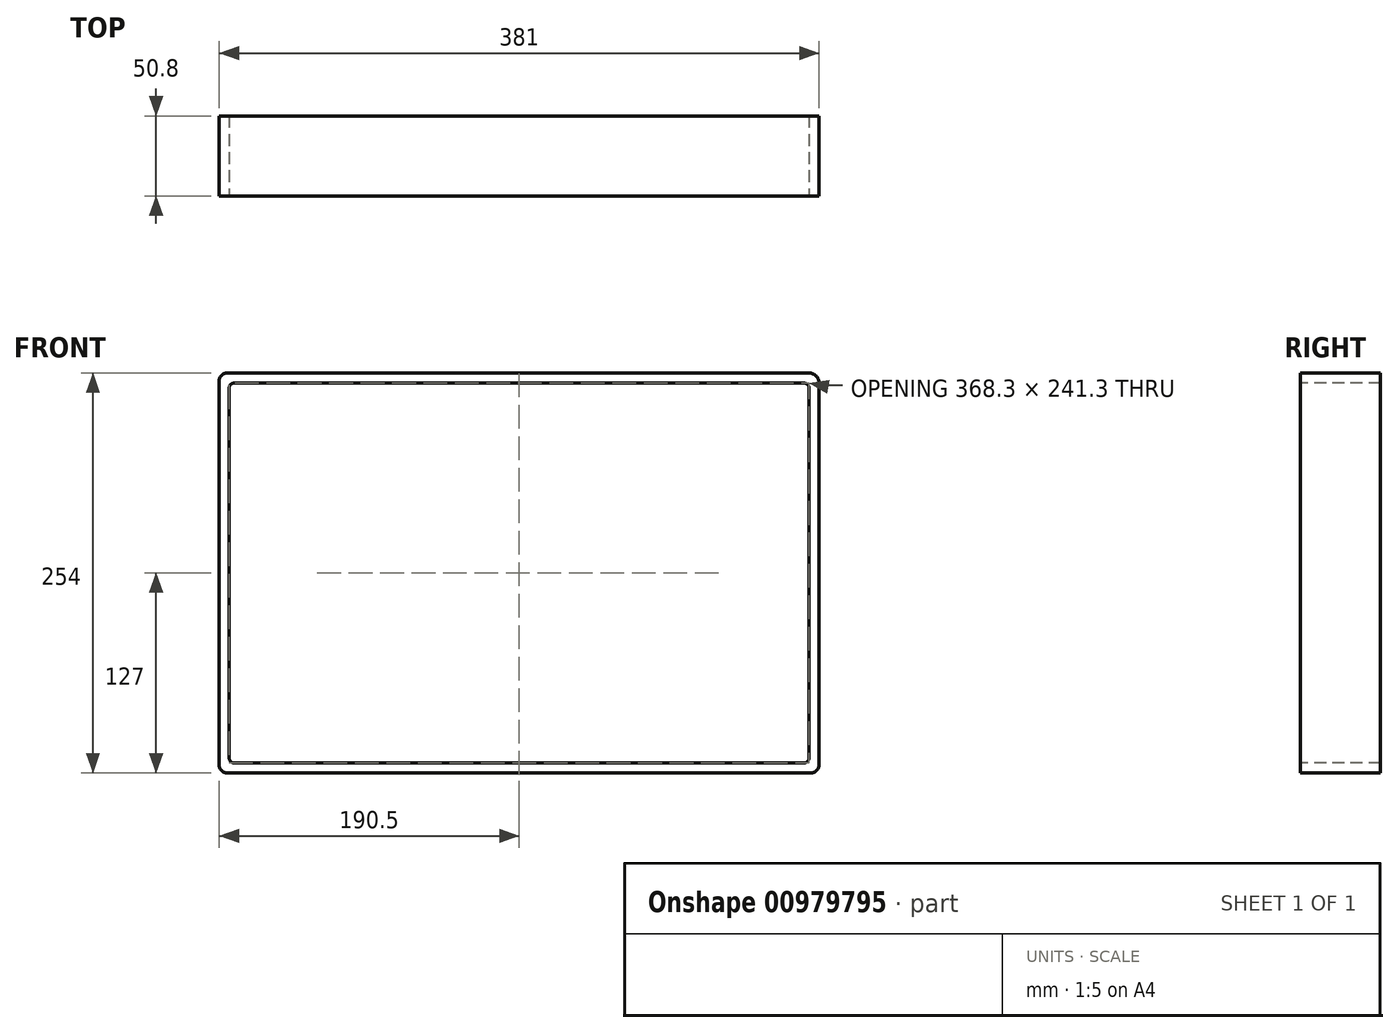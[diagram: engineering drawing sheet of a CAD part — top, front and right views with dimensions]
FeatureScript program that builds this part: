
annotation { "Feature Type Name" : "Feature", "Feature Type Description" : "" }
export const myFeature = defineFeature(function(context is Context, id is Id, definition is map)
    precondition{}
    {
        {
            var Q0;
            Q0=qCreatedBy(makeId("Front.planeOp"),FACE);
            var sketch = newSketch(context, id + "F0", { "sketchPlane" : qUnion([Q0])});
            skLineSegment(sketch, "E0.bottom", {"start": v(190.5, -127) * mm, "end": v(-190.5, -127) * mm});
            skLineSegment(sketch, "E0.top", {"start": v(190.5, 127) * mm, "end": v(-190.5, 127) * mm});
            skLineSegment(sketch, "E0.left", {"start": v(190.5, -127) * mm, "end": v(190.5, 127) * mm});
            skLineSegment(sketch, "E0.right", {"start": v(-190.5, -127) * mm, "end": v(-190.5, 127) * mm});
            skPoint(sketch, "E0.middle", {"position": v(0, 0) * mm});
            skSolve(sketch);
        }
        {
            var Q0;
            Q0=makeQuery(id+"F0.imprint","IMPRINT",FACE,{"disambiguationData":[TD([[makeQuery(id+"F0.imprint","IMPRINT",EDGE,{"derivedFrom":sQuery(id+"F0.wireOp",EDGE,"E0.bottom")}),-1.0]])]});
            extrude(context, id + "F1", {"entities" : qUnion([Q0]), "depth" : 50.8 * mm, "offsetDistance" : 25.4 * mm});
        }
        {
            var Q0;
            Q0=makeQuery(id+"F1.opExtrude","SWEPT_EDGE",EDGE,{"disambiguationData":[OSD([sQuery(id+"F0.wireOp",EDGE,"E0.top"),sQuery(id+"F0.wireOp",EDGE,"E0.left")])]});
            fillet(context, id + "F2", {"entities" : qUnion([Q0]), "radius" : 6.35 * mm, "tangentPropagation" : true, "allowEdgeOverflow" : false});
        }
        {
            var Q0;
            Q0=makeQuery(id+"F1.opExtrude","SWEPT_EDGE",EDGE,{"disambiguationData":[OSD([sQuery(id+"F0.wireOp",EDGE,"E0.bottom"),sQuery(id+"F0.wireOp",EDGE,"E0.left")])]});
            var Q1;
            Q1=makeQuery(id+"F1.opExtrude","SWEPT_EDGE",EDGE,{"disambiguationData":[OSD([sQuery(id+"F0.wireOp",EDGE,"E0.top"),sQuery(id+"F0.wireOp",EDGE,"E0.right")])]});
            var Q2;
            Q2=makeQuery(id+"F1.opExtrude","SWEPT_EDGE",EDGE,{"disambiguationData":[OSD([sQuery(id+"F0.wireOp",EDGE,"E0.bottom"),sQuery(id+"F0.wireOp",EDGE,"E0.right")])]});
            fillet(context, id + "F3", {"entities" : qUnion([Q0, Q1, Q2]), "radius" : 5.08 * mm, "tangentPropagation" : true, "allowEdgeOverflow" : false});
        }
        {
            var Q0;
            Q0=makeQuery(id+"F1.opExtrude","SWEPT_BODY",BODY,{"disambiguationData":[OSD([sQuery(id+"F0.wireOp",EDGE,"E0.bottom"),sQuery(id+"F0.wireOp",EDGE,"E0.top"),sQuery(id+"F0.wireOp",EDGE,"E0.left"),sQuery(id+"F0.wireOp",EDGE,"E0.right")])]});
            transform(context, id + "F4", {"entities" : qUnion([Q0]), "transformType" : TransformType.TRANSLATION_3D, "dx" : 0 * mm, "dy" : 50.8 * mm, "dz" : 0 * mm, "makeCopy" : false});
        }
        {
            var Q0;
            Q0=qCreatedBy(makeId("Front.planeOp"),FACE);
            var sketch = newSketch(context, id + "F5", { "sketchPlane" : qUnion([Q0])});
            skLineSegment(sketch, "E1.bottom", {"start": v(184.15, -120.65) * mm, "end": v(-184.15, -120.65) * mm});
            skLineSegment(sketch, "E1.top", {"start": v(184.15, 120.65) * mm, "end": v(-184.15, 120.65) * mm});
            skLineSegment(sketch, "E1.left", {"start": v(184.15, -120.65) * mm, "end": v(184.15, 120.65) * mm});
            skLineSegment(sketch, "E1.right", {"start": v(-184.15, -120.65) * mm, "end": v(-184.15, 120.65) * mm});
            skPoint(sketch, "E1.middle", {"position": v(0, 0) * mm});
            skSolve(sketch);
        }
        {
            var Q0;
            Q0=makeQuery(id+"F5.imprint","IMPRINT",FACE,{"disambiguationData":[TD([[makeQuery(id+"F5.imprint","IMPRINT",EDGE,{"derivedFrom":sQuery(id+"F5.wireOp",EDGE,"E1.bottom")}),-1.0]])]});
            extrude(context, id + "F6", {"entities" : qUnion([Q0]), "operationType" : NewBodyOperationType.REMOVE, "oppositeDirection" : true, "depth" : 50.8 * mm, "offsetDistance" : 25.4 * mm});
        }
        {
            var Q0;
            Q0=makeQuery(id+"F6.boolean.opBoolean","COPY",EDGE,{"derivedFrom":makeQuery(id+"F6.opExtrude","SWEPT_EDGE",EDGE,{"disambiguationData":[OSD([sQuery(id+"F5.wireOp",EDGE,"E1.bottom"),sQuery(id+"F5.wireOp",EDGE,"E1.right")])]})});
            var Q1;
            Q1=makeQuery(id+"F6.boolean.opBoolean","COPY",EDGE,{"derivedFrom":makeQuery(id+"F6.opExtrude","SWEPT_EDGE",EDGE,{"disambiguationData":[OSD([sQuery(id+"F5.wireOp",EDGE,"E1.top"),sQuery(id+"F5.wireOp",EDGE,"E1.right")])]})});
            var Q2;
            Q2=makeQuery(id+"F6.boolean.opBoolean","COPY",EDGE,{"derivedFrom":makeQuery(id+"F6.opExtrude","SWEPT_EDGE",EDGE,{"disambiguationData":[OSD([sQuery(id+"F5.wireOp",EDGE,"E1.bottom"),sQuery(id+"F5.wireOp",EDGE,"E1.left")])]})});
            var Q3;
            Q3=makeQuery(id+"F6.boolean.opBoolean","COPY",EDGE,{"derivedFrom":makeQuery(id+"F6.opExtrude","SWEPT_EDGE",EDGE,{"disambiguationData":[OSD([sQuery(id+"F5.wireOp",EDGE,"E1.top"),sQuery(id+"F5.wireOp",EDGE,"E1.left")])]})});
            fillet(context, id + "F7", {"entities" : qUnion([Q0, Q1, Q2, Q3]), "radius" : 3.17 * mm, "tangentPropagation" : true, "allowEdgeOverflow" : false});
        }
        {
            var Q0;
            Q0=makeQuery(id+"F1.opExtrude","SWEPT_BODY",BODY,{"disambiguationData":[OSD([sQuery(id+"F0.wireOp",EDGE,"E0.bottom"),sQuery(id+"F0.wireOp",EDGE,"E0.top"),sQuery(id+"F0.wireOp",EDGE,"E0.left"),sQuery(id+"F0.wireOp",EDGE,"E0.right")])]});
            transform(context, id + "F8", {"entities" : qUnion([Q0]), "transformType" : TransformType.TRANSLATION_3D, "dx" : 0 * mm, "dy" : 50.8 * mm, "dz" : 0 * mm, "makeCopy" : false});
        }
        {
            var Q0;
            Q0=makeQuery(id+"F1.opExtrude","SWEPT_BODY",BODY,{"disambiguationData":[OSD([sQuery(id+"F0.wireOp",EDGE,"E0.bottom"),sQuery(id+"F0.wireOp",EDGE,"E0.top"),sQuery(id+"F0.wireOp",EDGE,"E0.left"),sQuery(id+"F0.wireOp",EDGE,"E0.right")])]});
            transform(context, id + "F9", {"entities" : qUnion([Q0]), "transformType" : TransformType.TRANSLATION_3D, "dx" : 0 * mm, "dy" : 203.2 * mm, "dz" : 0 * mm, "makeCopy" : false});
        }
    });
